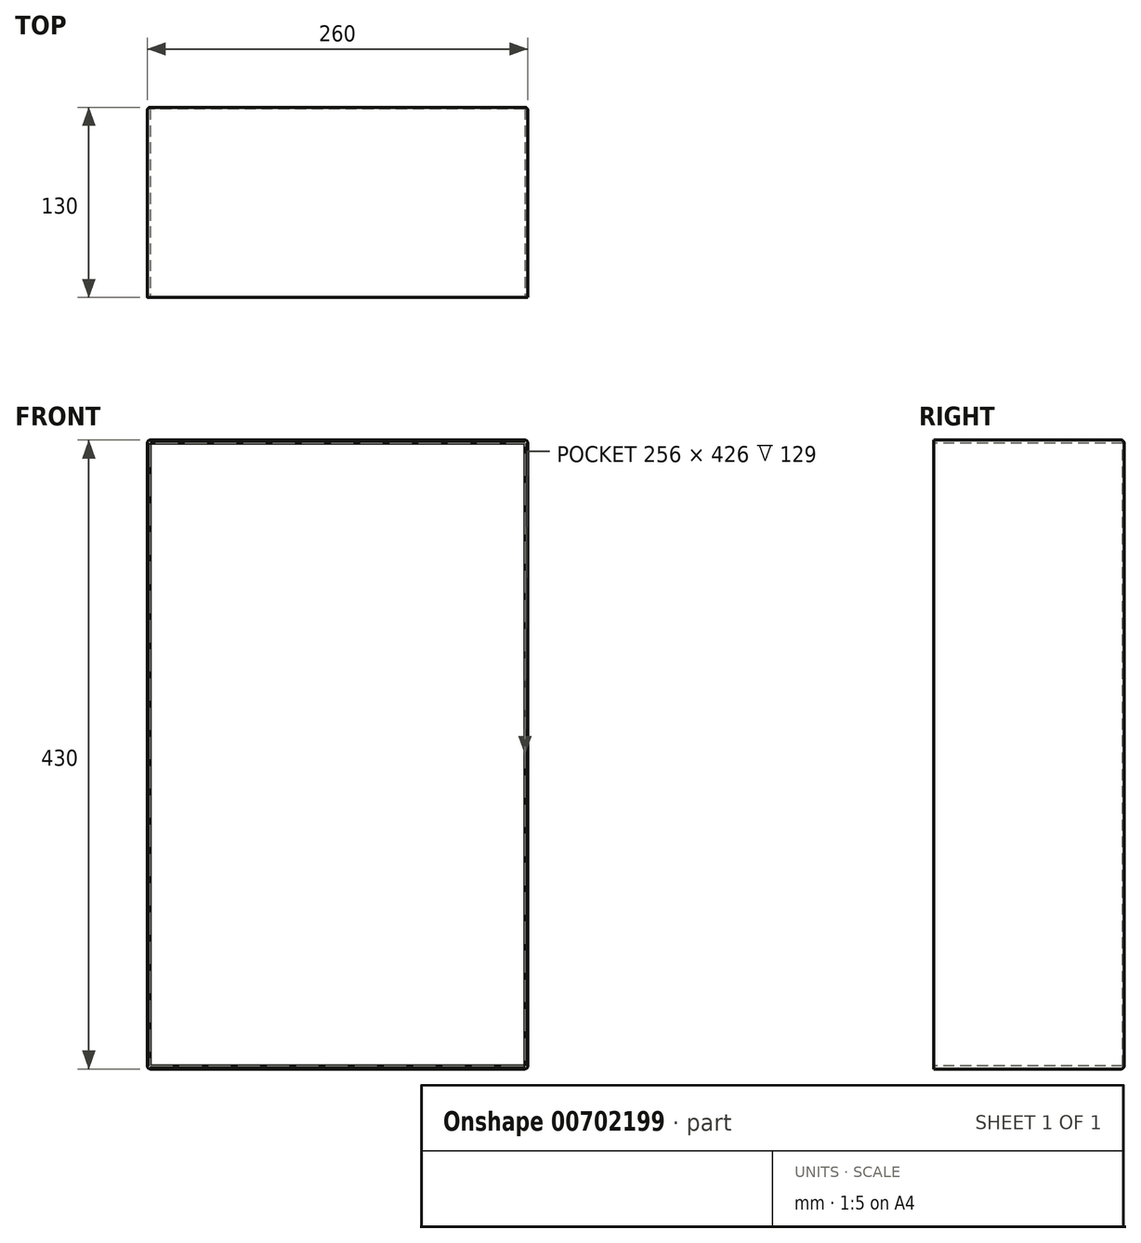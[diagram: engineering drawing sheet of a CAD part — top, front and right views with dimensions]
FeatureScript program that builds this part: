
annotation { "Feature Type Name" : "Feature", "Feature Type Description" : "" }
export const myFeature = defineFeature(function(context is Context, id is Id, definition is map)
    precondition{}
    {
        {
            var Q0;
            Q0=qCreatedBy(makeId("Front.planeOp"),FACE);
            var sketch = newSketch(context, id + "F0", { "sketchPlane" : qUnion([Q0])});
            skLineSegment(sketch, "E0.bottom", {"start": v(130, -215) * mm, "end": v(-130, -215) * mm});
            skLineSegment(sketch, "E0.top", {"start": v(130, 215) * mm, "end": v(-130, 215) * mm});
            skLineSegment(sketch, "E0.left", {"start": v(130, -215) * mm, "end": v(130, 215) * mm});
            skLineSegment(sketch, "E0.right", {"start": v(-130, -215) * mm, "end": v(-130, 215) * mm});
            skPoint(sketch, "E0.middle", {"position": v(0, 0) * mm});
            skSolve(sketch);
        }
        {
            var Q0;
            Q0=makeQuery(id+"F0.imprint","IMPRINT",FACE,{"disambiguationData":[TD([[makeQuery(id+"F0.imprint","IMPRINT",EDGE,{"derivedFrom":sQuery(id+"F0.wireOp",EDGE,"E0.bottom")}),-1.0]])]});
            extrude(context, id + "F1", {"entities" : qUnion([Q0]), "depth" : 130 * mm, "offsetDistance" : 25 * mm});
        }
        {
            var Q0;
            Q0=makeQuery(id+"F1.opExtrude","CAP_FACE",FACE,{"disambiguationData":[OSD([sQuery(id+"F0.wireOp",EDGE,"E0.bottom"),sQuery(id+"F0.wireOp",EDGE,"E0.top"),sQuery(id+"F0.wireOp",EDGE,"E0.left"),sQuery(id+"F0.wireOp",EDGE,"E0.right")])],"isStart":false});
            var sketch = newSketch(context, id + "F2", { "sketchPlane" : qUnion([Q0])});
            skLineSegment(sketch, "E1.bottom", {"start": v(128, -213) * mm, "end": v(-128, -213) * mm});
            skLineSegment(sketch, "E1.top", {"start": v(128, 213) * mm, "end": v(-128, 213) * mm});
            skLineSegment(sketch, "E1.left", {"start": v(128, -213) * mm, "end": v(128, 213) * mm});
            skLineSegment(sketch, "E1.right", {"start": v(-128, -213) * mm, "end": v(-128, 213) * mm});
            skPoint(sketch, "E1.middle", {"position": v(0, 0) * mm});
            skSolve(sketch);
        }
        {
            var Q0;
            Q0=makeQuery(id+"F2.imprint","IMPRINT",FACE,{"disambiguationData":[TD([[makeQuery(id+"F2.imprint","IMPRINT",EDGE,{"derivedFrom":sQuery(id+"F2.wireOp",EDGE,"E1.bottom")}),-1.0]])]});
            extrude(context, id + "F3", {"entities" : qUnion([Q0]), "operationType" : NewBodyOperationType.REMOVE, "oppositeDirection" : true, "depth" : 129 * mm, "offsetDistance" : 25 * mm});
        }
        {
            var Q0;
            Q0=makeQuery(id+"F1.opExtrude","SWEPT_EDGE",EDGE,{"disambiguationData":[OSD([sQuery(id+"F0.wireOp",EDGE,"E0.top"),sQuery(id+"F0.wireOp",EDGE,"E0.right")])]});
            var Q1;
            Q1=makeQuery(id+"F1.opExtrude","SWEPT_EDGE",EDGE,{"disambiguationData":[OSD([sQuery(id+"F0.wireOp",EDGE,"E0.top"),sQuery(id+"F0.wireOp",EDGE,"E0.left")])]});
            var Q2;
            Q2=makeQuery(id+"F1.opExtrude","SWEPT_EDGE",EDGE,{"disambiguationData":[OSD([sQuery(id+"F0.wireOp",EDGE,"E0.bottom"),sQuery(id+"F0.wireOp",EDGE,"E0.right")])]});
            var Q3;
            Q3=makeQuery(id+"F1.opExtrude","SWEPT_EDGE",EDGE,{"disambiguationData":[OSD([sQuery(id+"F0.wireOp",EDGE,"E0.bottom"),sQuery(id+"F0.wireOp",EDGE,"E0.left")])]});
            var Q4;
            Q4=makeQuery(id+"F1.opExtrude","CAP_EDGE",EDGE,{"disambiguationData":[OSD([sQuery(id+"F0.wireOp",EDGE,"E0.bottom")])],"isStart":true});
            var Q5;
            Q5=makeQuery(id+"F1.opExtrude","CAP_EDGE",EDGE,{"disambiguationData":[OSD([sQuery(id+"F0.wireOp",EDGE,"E0.left")])],"isStart":true});
            var Q6;
            Q6=makeQuery(id+"F1.opExtrude","CAP_EDGE",EDGE,{"disambiguationData":[OSD([sQuery(id+"F0.wireOp",EDGE,"E0.right")])],"isStart":true});
            var Q7;
            Q7=makeQuery(id+"F1.opExtrude","CAP_EDGE",EDGE,{"disambiguationData":[OSD([sQuery(id+"F0.wireOp",EDGE,"E0.top")])],"isStart":true});
            fillet(context, id + "F4", {"entities" : qUnion([Q0, Q1, Q2, Q3, Q4, Q5, Q6, Q7]), "radius" : 2 * mm, "tangentPropagation" : true, "allowEdgeOverflow" : false});
        }
    });
